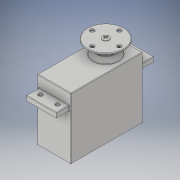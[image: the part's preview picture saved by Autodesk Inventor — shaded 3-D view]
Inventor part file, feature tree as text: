
AUTODESK INVENTOR PART (.ipt)
format: ipt  version: 2019 (Build 230136000, 136)  size: 359,424 bytes
history: native  units: mm
features: sketch x10, extrude x8, other x5, projected_geometry x3, loft x1, revolve x1, pattern_linear x1, fillet x1
ambient origin geometry x8: Origin, YZ Plane, XZ Plane, XY Plane, X Axis, Y Axis, Z Axis, Center Point
bodies: Body1 (feature_tree)
feature tree (30):
  other  "Твердое тело1"
  extrude  "Выдавливание1"  Depth=19.8mm
  other  "РабПлоскость1"
  extrude  "Выдавливание2"  Depth=42.3mm
  sketch  "Эскиз3"
  other  "РабПлоскость2"
  loft  "Лофт1"
  other  "РабПлоскость3"
  extrude  "Выдавливание3"  [1 undecoded]
  sketch  "Эскиз6"
  extrude  "Выдавливание4"  Depth=57.5mm
  extrude  "Выдавливание5"  Depth=3.0mm TaperAngle=0.0deg
  sketch  "Эскиз7"
  other  "РабПлоскость4"
  revolve  "Вращение1"
  extrude  "Выдавливание6"  Depth=1.0mm
  extrude  "Выдавливание7"  Depth=15.0mm
  extrude  "Выдавливание8"  Depth=3.0mm
  pattern_linear  "Прямоуг.массив1"  Spacing1=11.5mm  [1 undecoded]
  fillet  "Сопряжение1"  [1 undecoded]
  sketch  "Эскиз1"
  sketch  "Эскиз2"
  sketch  "Эскиз4"
  sketch  "Эскиз5"
  projected_geometry  "Спроецированная петля1"
  projected_geometry  "Спроецированная петля2"
  sketch  "Эскиз8"
  sketch  "Эскиз9"
  projected_geometry  "Спроецированная петля3"
  sketch  "Эскиз10"
note: 3 required parameter values undecoded (feature->parameter linkage not recoverable at this tier; creation-order binding heuristic only, values carry confidence <= 0.55)
